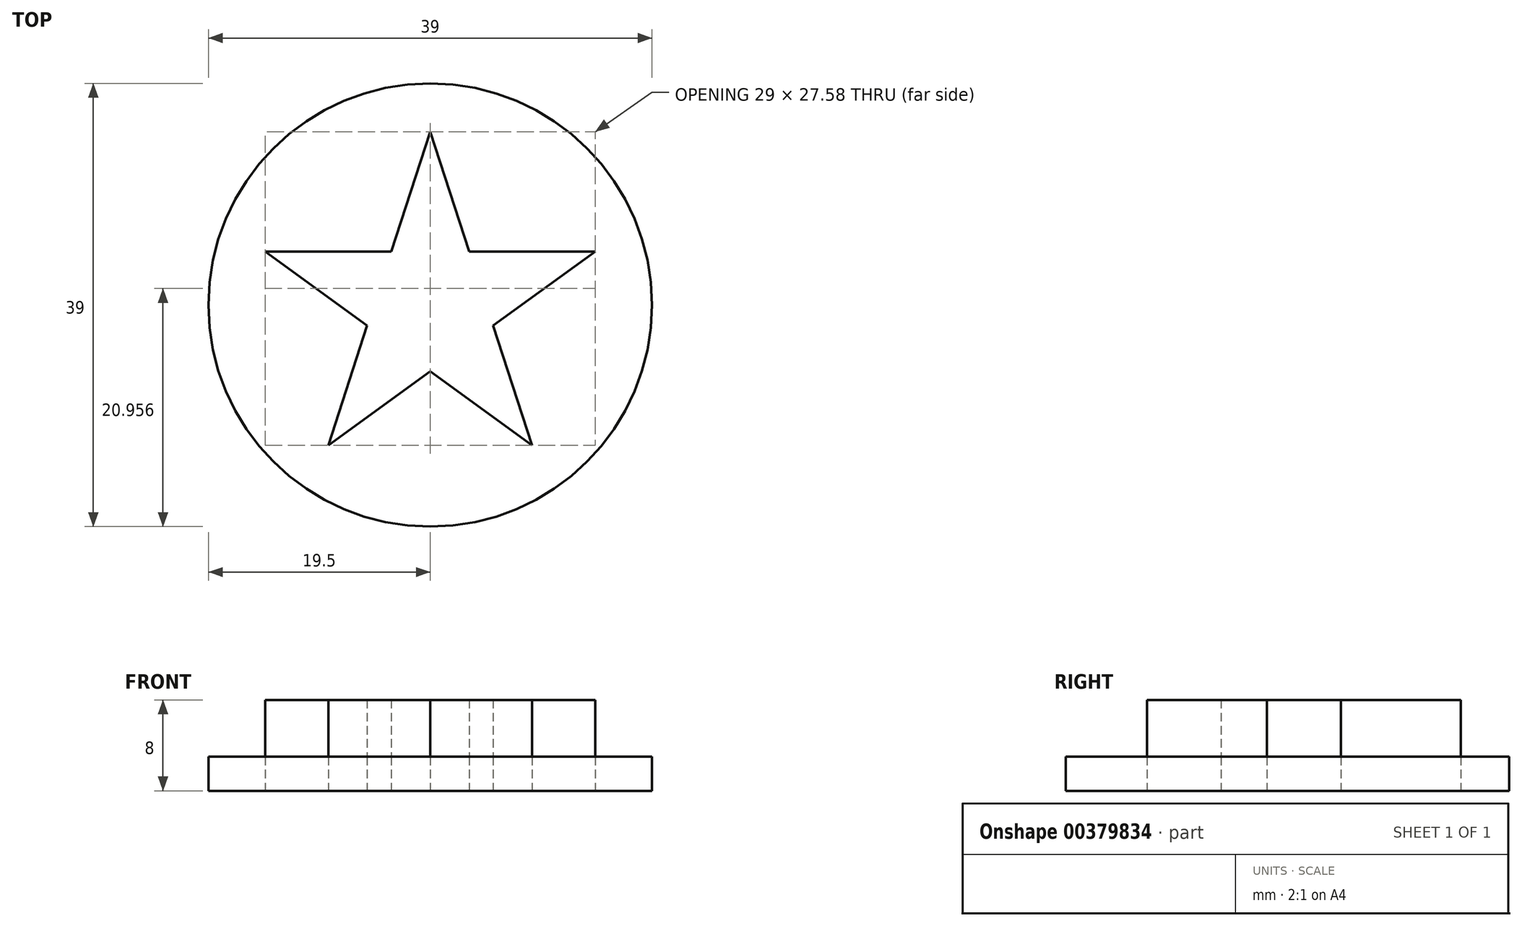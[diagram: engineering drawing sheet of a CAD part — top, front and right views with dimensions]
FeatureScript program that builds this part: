
annotation { "Feature Type Name" : "Feature", "Feature Type Description" : "" }
export const myFeature = defineFeature(function(context is Context, id is Id, definition is map)
    precondition{}
    {
        {
            var Q0;
            Q0=qCreatedBy(makeId("Top.planeOp"),FACE);
            var sketch = newSketch(context, id + "F0", { "sketchPlane" : qUnion([Q0])});
            skLineSegment(sketch, "E0", {"start": v(-8.96, -12.33) * mm, "end": v(0, 15.25) * mm});
            skLineSegment(sketch, "E1", {"start": v(0, 15.25) * mm, "end": v(8.96, -12.33) * mm});
            skLineSegment(sketch, "E2", {"start": v(8.96, -12.33) * mm, "end": v(-14.5, 4.71) * mm});
            skLineSegment(sketch, "E3", {"start": v(-14.5, 4.71) * mm, "end": v(14.5, 4.71) * mm});
            skLineSegment(sketch, "E4", {"start": v(14.5, 4.71) * mm, "end": v(-8.96, -12.33) * mm});
            skLineSegment(sketch, "E5", {"start": v(0, -5.82) * mm, "end": v(0, 4.71) * mm, "construction": true});
            skCircle(sketch, "E6", {"center": v(0, 0) * mm, "radius": 19.5 * mm});
            skLineSegment(sketch, "E7", {"start": v(5.54, -1.8) * mm, "end": v(-4.48, 1.46) * mm, "construction": true});
            skLineSegment(sketch, "E8", {"start": v(3.42, 4.71) * mm, "end": v(-2.77, -3.81) * mm, "construction": true});
            skLineSegment(sketch, "E9", {"start": v(-3.42, 4.71) * mm, "end": v(2.77, -3.81) * mm, "construction": true});
            skLineSegment(sketch, "E10", {"start": v(-5.54, -1.8) * mm, "end": v(4.48, 1.46) * mm, "construction": true});
            skSolve(sketch);
        }
        {
            var Q0;
            Q0=makeQuery(id+"F0.imprint","IMPRINT",FACE,{"disambiguationData":[TD([[makeQuery(id+"F0.imprint","IMPRINT",EDGE,{"derivedFrom":sQuery(id+"F0.wireOp",EDGE,"E6")}),1.0]])]});
            extrude(context, id + "F1", {"entities" : qUnion([Q0]), "depth" : 3 * mm});
        }
        {
            var Q0;
            Q0=makeQuery(id+"F1.opExtrude","CAP_FACE",FACE,{"disambiguationData":[OSD([sQuery(id+"F0.wireOp",EDGE,"E0"),sQuery(id+"F0.wireOp",EDGE,"E1"),sQuery(id+"F0.wireOp",EDGE,"E2"),sQuery(id+"F0.wireOp",EDGE,"E3"),sQuery(id+"F0.wireOp",EDGE,"E4"),sQuery(id+"F0.wireOp",EDGE,"E6")])],"isStart":false});
            var sketch = newSketch(context, id + "F2", { "sketchPlane" : qUnion([Q0])});
            skLineSegment(sketch, "E11", {"start": v(-3.42, 4.71) * mm, "end": v(0, 15.25) * mm});
            skLineSegment(sketch, "E12", {"start": v(0, 15.25) * mm, "end": v(3.42, 4.71) * mm});
            skLineSegment(sketch, "E13", {"start": v(3.42, 4.71) * mm, "end": v(14.5, 4.71) * mm});
            skLineSegment(sketch, "E14", {"start": v(14.5, 4.71) * mm, "end": v(5.54, -1.8) * mm});
            skLineSegment(sketch, "E15", {"start": v(5.54, -1.8) * mm, "end": v(8.96, -12.33) * mm});
            skLineSegment(sketch, "E16", {"start": v(8.96, -12.33) * mm, "end": v(0, -5.82) * mm});
            skLineSegment(sketch, "E17", {"start": v(0, -5.82) * mm, "end": v(-8.96, -12.33) * mm});
            skLineSegment(sketch, "E18", {"start": v(-8.96, -12.33) * mm, "end": v(-5.54, -1.8) * mm});
            skLineSegment(sketch, "E19", {"start": v(-5.54, -1.8) * mm, "end": v(-14.5, 4.71) * mm});
            skLineSegment(sketch, "E20", {"start": v(-14.5, 4.71) * mm, "end": v(-3.42, 4.71) * mm});
            skSolve(sketch);
        }
        {
            var Q0;
            Q0 = qSketchRegion(id + "F2", true);
            extrude(context, id + "F3", {"entities" : qUnion([Q0]), "depth" : 5 * mm});
        }
    });
